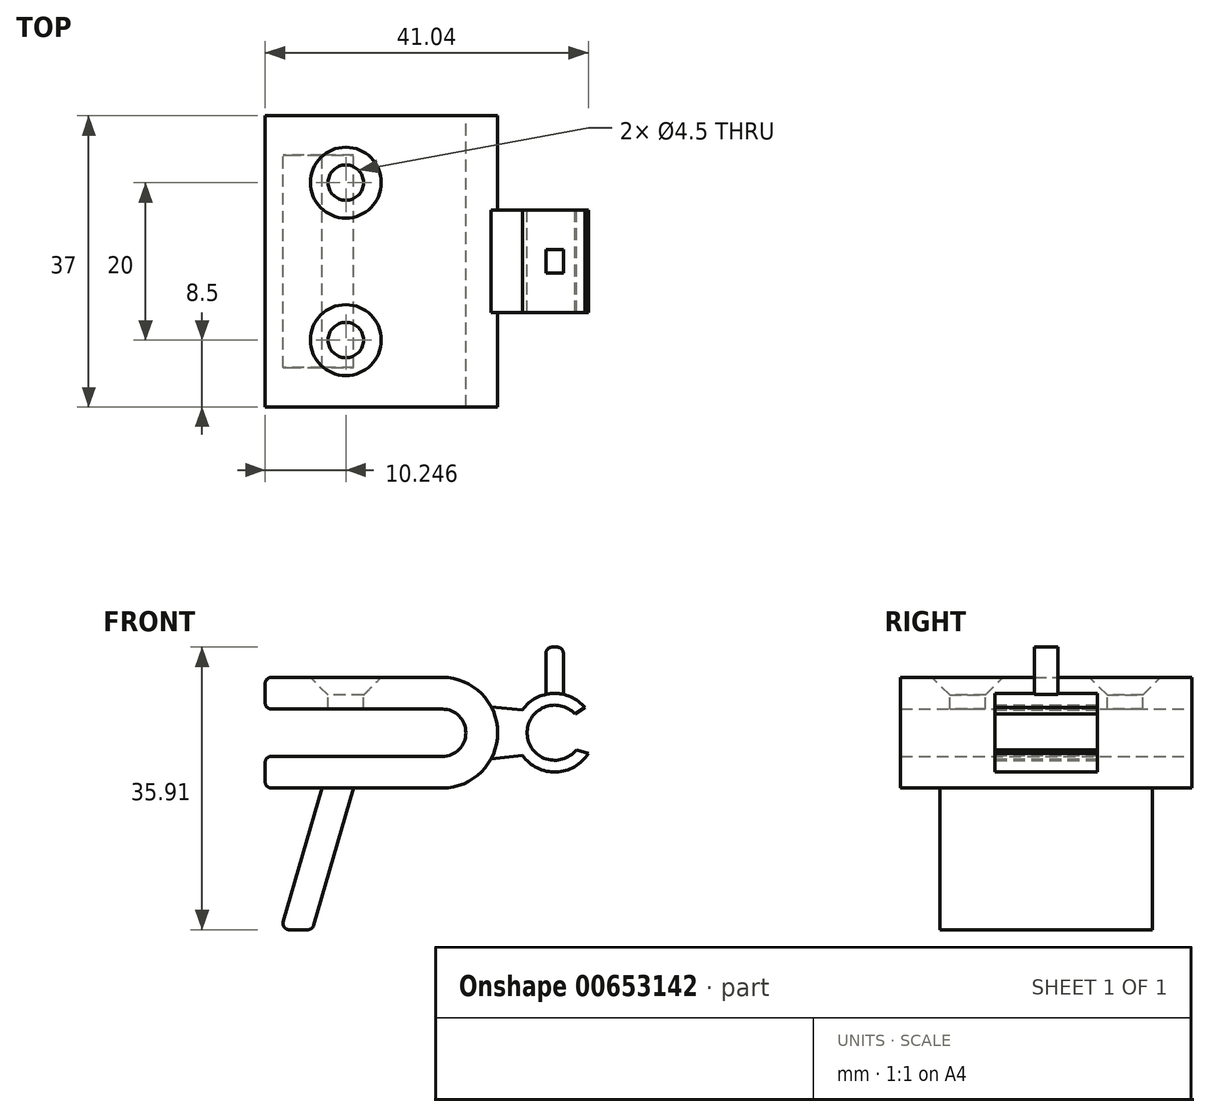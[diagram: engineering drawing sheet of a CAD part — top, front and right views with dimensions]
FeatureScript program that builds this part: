
annotation { "Feature Type Name" : "Feature", "Feature Type Description" : "" }
export const myFeature = defineFeature(function(context is Context, id is Id, definition is map)
    precondition{}
    {
        {
            var Q0;
            Q0=qCreatedBy(makeId("Front.planeOp"),FACE);
            var sketch = newSketch(context, id + "F0", { "sketchPlane" : qUnion([Q0])});
            skLineSegment(sketch, "E0", {"start": v(2.65, 19.1) * mm, "end": v(-19.05, 19.1) * mm});
            skLineSegment(sketch, "E1", {"start": v(2.65, 33.15) * mm, "end": v(-19.05, 33.15) * mm});
            skLineSegment(sketch, "E2", {"start": v(-19.85, 32.35) * mm, "end": v(-19.85, 29.92) * mm});
            skLineSegment(sketch, "E3", {"start": v(-19.05, 29.12) * mm, "end": v(2.65, 29.12) * mm});
            skLineSegment(sketch, "E4", {"start": v(-19.05, 23.12) * mm, "end": v(2.65, 23.12) * mm});
            skLineSegment(sketch, "E5", {"start": v(-19.85, 22.32) * mm, "end": v(-19.85, 19.9) * mm});
            skArc(sketch, "E6", {"start": v(2.65, 19.1) * mm, "mid": v(9.68, 26.12) * mm, "end": v(2.65, 33.15) * mm});
            skArc(sketch, "E7", {"start": v(2.65, 23.12) * mm, "mid": v(5.65, 26.12) * mm, "end": v(2.65, 29.12) * mm});
            skLineSegment(sketch, "E8", {"start": v(8.85, 29.42) * mm, "end": v(12.86, 29.03) * mm});
            skArc(sketch, "E9", {"start": v(20.77, 29.31) * mm, "mid": v(11.93, 25.77) * mm, "end": v(21.19, 23.51) * mm});
            skLineSegment(sketch, "E10.MirrorCS", {"start": v(8.85, 22.82) * mm, "end": v(12.86, 23.21) * mm});
            skArc(sketch, "E11", {"start": v(19.5, 28.5) * mm, "mid": v(13.42, 25.98) * mm, "end": v(19.68, 23.96) * mm});
            skLineSegment(sketch, "E12", {"start": v(19.5, 28.5) * mm, "end": v(20.77, 29.31) * mm});
            skLineSegment(sketch, "E13", {"start": v(19.68, 23.96) * mm, "end": v(21.19, 23.51) * mm});
            skLineSegment(sketch, "E14", {"start": v(15.82, 31) * mm, "end": v(15.82, 36.2) * mm});
            skLineSegment(sketch, "E15", {"start": v(16.62, 37) * mm, "end": v(17.23, 37) * mm});
            skLineSegment(sketch, "E16", {"start": v(18.03, 36.2) * mm, "end": v(18.03, 31) * mm});
            skLineSegment(sketch, "E17", {"start": v(-12.6, 19.1) * mm, "end": v(-17.56, 2.12) * mm});
            skLineSegment(sketch, "E18", {"start": v(-16.79, 1.1) * mm, "end": v(-14.46, 1.1) * mm});
            skLineSegment(sketch, "E19", {"start": v(-13.69, 1.67) * mm, "end": v(-8.6, 19.1) * mm});
            skPoint(sketch, "E20.visualSharp", {"position": v(-17.86, 1.1) * mm});
            skArc(sketch, "E20.filletArc", {"start": v(-17.56, 2.12) * mm, "mid": v(-17.43, 1.41) * mm, "end": v(-16.79, 1.1) * mm});
            skPoint(sketch, "E21.visualSharp", {"position": v(-13.86, 1.1) * mm});
            skArc(sketch, "E21.filletArc", {"start": v(-14.46, 1.1) * mm, "mid": v(-13.98, 1.25) * mm, "end": v(-13.69, 1.67) * mm});
            skPoint(sketch, "E22.visualSharp", {"position": v(-19.85, 23.12) * mm});
            skArc(sketch, "E22.filletArc", {"start": v(-19.05, 23.12) * mm, "mid": v(-19.62, 22.89) * mm, "end": v(-19.85, 22.32) * mm});
            skPoint(sketch, "E23.visualSharp", {"position": v(-19.85, 19.1) * mm});
            skArc(sketch, "E23.filletArc", {"start": v(-19.85, 19.9) * mm, "mid": v(-19.62, 19.33) * mm, "end": v(-19.05, 19.1) * mm});
            skPoint(sketch, "E24.visualSharp", {"position": v(-19.85, 29.12) * mm});
            skArc(sketch, "E24.filletArc", {"start": v(-19.85, 29.92) * mm, "mid": v(-19.62, 29.36) * mm, "end": v(-19.05, 29.12) * mm});
            skPoint(sketch, "E25.visualSharp", {"position": v(-19.85, 33.15) * mm});
            skArc(sketch, "E25.filletArc", {"start": v(-19.05, 33.15) * mm, "mid": v(-19.62, 32.92) * mm, "end": v(-19.85, 32.35) * mm});
            skPoint(sketch, "E26.visualSharp", {"position": v(15.82, 37) * mm});
            skArc(sketch, "E26.filletArc", {"start": v(16.62, 37) * mm, "mid": v(16.05, 36.76) * mm, "end": v(15.82, 36.2) * mm});
            skPoint(sketch, "E27.visualSharp", {"position": v(18.03, 37) * mm});
            skArc(sketch, "E27.filletArc", {"start": v(18.03, 36.2) * mm, "mid": v(17.8, 36.76) * mm, "end": v(17.23, 37) * mm});
            skSolve(sketch);
        }
        {
            var Q0;
            {var subQ8=sQuery(id+"F0.wireOp",EDGE,"E1");Q0=makeQuery(id+"F0.imprint","IMPRINT",FACE,{"disambiguationData":[TD([[makeQuery(id+"F0.imprint","IMPRINT",EDGE,{"derivedFrom":subQ8}),1.0]])]});}
            extrude(context, id + "F1", {"entities" : qUnion([Q0]), "endBound" : BoundingType.SYMMETRIC, "depth" : 37 * mm, "offsetDistance" : 25 * mm});
        }
        {
            var Q0;
            {var subQ0=sQuery(id+"F0.wireOp",EDGE,"E8");Q0=makeQuery(id+"F0.imprint","IMPRINT",FACE,{"disambiguationData":[TD([[makeQuery(id+"F0.imprint","IMPRINT",EDGE,{"derivedFrom":subQ0}),-1.0]])]});}
            var Q1;
            Q1=makeQuery(id+"F0.imprint","IMPRINT",FACE,{"disambiguationData":[TD([[makeQuery(id+"F0.imprint","IMPRINT",EDGE,{"derivedFrom":sQuery(id+"F0.wireOp",EDGE,"E11")}),-1.0]])]});
            extrude(context, id + "F2", {"entities" : qUnion([Q0, Q1]), "operationType" : NewBodyOperationType.ADD, "endBound" : BoundingType.SYMMETRIC, "depth" : 13 * mm, "offsetDistance" : 25 * mm});
        }
        {
            var Q0;
            {var subQ0=sQuery(id+"F0.wireOp",EDGE,"E14");Q0=makeQuery(id+"F0.imprint","IMPRINT",FACE,{"disambiguationData":[TD([[makeQuery(id+"F0.imprint","IMPRINT",EDGE,{"derivedFrom":subQ0}),-1.0]])]});}
            extrude(context, id + "F3", {"entities" : qUnion([Q0]), "operationType" : NewBodyOperationType.ADD, "endBound" : BoundingType.SYMMETRIC, "depth" : 3 * mm, "offsetDistance" : 25 * mm});
        }
        {
            var Q0;
            {var subQ1=sQuery(id+"F0.wireOp",EDGE,"E17");Q0=makeQuery(id+"F0.imprint","IMPRINT",FACE,{"disambiguationData":[TD([[makeQuery(id+"F0.imprint","IMPRINT",EDGE,{"derivedFrom":subQ1}),1.0]])]});}
            extrude(context, id + "F4", {"entities" : qUnion([Q0]), "operationType" : NewBodyOperationType.ADD, "endBound" : BoundingType.SYMMETRIC, "depth" : 27 * mm, "offsetDistance" : 25 * mm});
        }
        {
            var Q0;
            Q0=makeQuery(id+"F1.opExtrude","SWEPT_FACE",FACE,{"disambiguationData":[OSD([sQuery(id+"F0.wireOp",EDGE,"E1")])]});
            var sketch = newSketch(context, id + "F5", { "sketchPlane" : qUnion([Q0])});
            skCircle(sketch, "E28", {"center": v(-9.6, 10) * mm, "radius": 2.25 * mm});
            skCircle(sketch, "E29", {"center": v(-9.6, -10) * mm, "radius": 2.25 * mm});
            skSolve(sketch);
        }
        {
            var Q0;
            Q0=sQuery(id+"F5.wireOp",VERTEX,"E28.center");
            var Q1;
            Q1=sQuery(id+"F5.wireOp",VERTEX,"E29.center");
            var Q2;
            Q2=makeQuery(id+"F1.opExtrude","SWEPT_BODY",BODY,{"disambiguationData":[OSD([sQuery(id+"F0.wireOp",EDGE,"E0"),sQuery(id+"F0.wireOp",EDGE,"E1"),sQuery(id+"F0.wireOp",EDGE,"E2"),sQuery(id+"F0.wireOp",EDGE,"E3"),sQuery(id+"F0.wireOp",EDGE,"E4"),sQuery(id+"F0.wireOp",EDGE,"E5"),sQuery(id+"F0.wireOp",EDGE,"E6"),sQuery(id+"F0.wireOp",EDGE,"E7"),sQuery(id+"F0.wireOp",EDGE,"E22.filletArc"),sQuery(id+"F0.wireOp",EDGE,"E23.filletArc"),sQuery(id+"F0.wireOp",EDGE,"E24.filletArc"),sQuery(id+"F0.wireOp",EDGE,"E25.filletArc")])]});
            hole(context, id + "F6", {"style" : HoleStyle.C_SINK, "endStyle" : HoleEndStyle.BLIND, "holeDiameter" : 4.5 * mm, "cSinkDiameter" : 9 * mm, "cSinkAngle" : 90 * degree, "majorDiameter" : 5 * mm, "holeDepth" : 7 * mm, "isTappedThrough" : true, "tappedDepth" : 12 * mm, "tapClearance" : 3, "locations" : qUnion([Q0, Q1]), "scope" : qUnion([Q2])});
        }
    });
